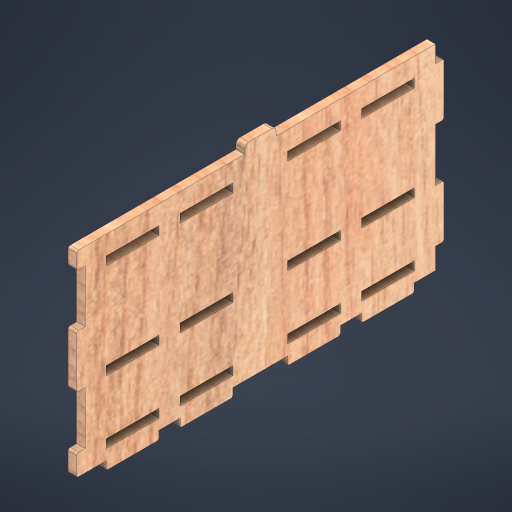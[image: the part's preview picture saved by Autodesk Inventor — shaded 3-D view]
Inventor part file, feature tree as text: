
AUTODESK INVENTOR PART (.ipt)
format: ipt  version: 2024.1 (Build 281209000, 209)  size: 568,832 bytes
history: native  units: mm
features: extrude x1, fillet x1, sketch x1
ambient origin geometry x8: Origin, YZ Plane, XZ Plane, XY Plane, X Axis, Y Axis, Z Axis, Center Point
bodies: Solid1 (feature_tree)
feature tree (3):
  extrude  "Extrusion1"  Depth=25.0mm
  fillet  "Fillet1"  Radius=25.0mm
  sketch  "Sketch1"  dims[d0=4.0mm d1=25.0mm d2=25.0mm d3=10.0mm d4=4.0mm d5=13.0mm d14=75.0mm d15=20.0mm d17=75.0mm d18=10.0mm d20=10.0mm d22=20.0mm d24=45.0mm d25=10.0mm d27=10.0mm d29=9.0mm d30=5.0mm d31=10.0mm d32=10.0mm d33=25.0mm d34=25.0mm d35=25.0mm d36=10.0mm d37=20.0mm d39=9.0mm d40=10.0mm d42=10.0mm d44=4.0mm d45=0.0mm d46=15.0mm d47=4.0mm d48=2.0mm d49=2.0mm d50=1.0mm]
